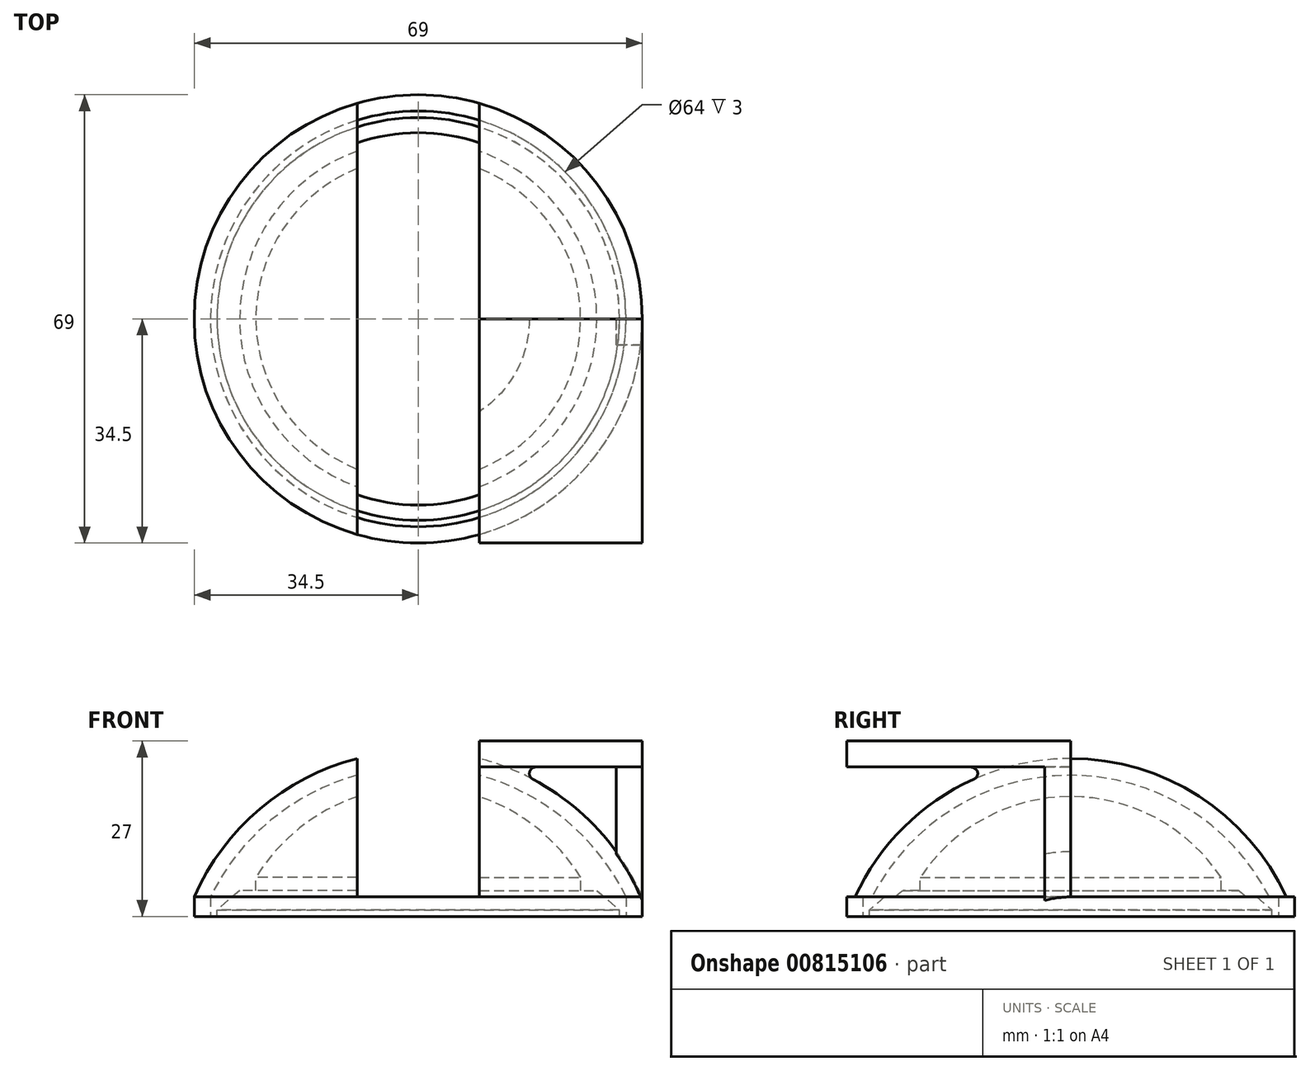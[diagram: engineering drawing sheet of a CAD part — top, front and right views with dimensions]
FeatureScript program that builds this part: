
annotation { "Feature Type Name" : "Feature", "Feature Type Description" : "" }
export const myFeature = defineFeature(function(context is Context, id is Id, definition is map)
    precondition{}
    {
        {
            var Q0;
            Q0=qCreatedBy(makeId("Front.planeOp"),FACE);
            var sketch = newSketch(context, id + "F0", { "sketchPlane" : qUnion([Q0])});
            skLineSegment(sketch, "E0", {"start": v(0, 0) * mm, "end": v(-31, 0) * mm});
            skLineSegment(sketch, "E1", {"start": v(-25, 4) * mm, "end": v(-27.5, 4) * mm});
            skLineSegment(sketch, "E2", {"start": v(-31, 0) * mm, "end": v(-31, 1) * mm});
            skLineSegment(sketch, "E3", {"start": v(-31, 1) * mm, "end": v(-27.5, 4) * mm});
            skLineSegment(sketch, "E4", {"start": v(-25, 4) * mm, "end": v(-25, 6) * mm});
            skArc(sketch, "E5.trimOffspring", {"start": v(0, 20) * mm, "mid": v(-14.33, 16.26) * mm, "end": v(-25, 6) * mm});
            skLineSegment(sketch, "E6", {"start": v(0, 20) * mm, "end": v(0, 0) * mm});
            skSolve(sketch);
        }
        {
            var Q0;
            Q0 = qSketchRegion(id + "F0", true);
            var Q1;
            Q1=sQuery(id+"F0.wireOp",EDGE,"E6");
            revolve(context, id + "F1", {"surfaceOperationType" : NewSurfaceOperationType.NEW, "entities" : qUnion([Q0]), "axis" : qUnion([Q1]), "revolveType" : RevolveType.FULL});
        }
        {
            var Q0;
            Q0=qCreatedBy(makeId("Top.planeOp"),FACE);
            var sketch = newSketch(context, id + "F2", { "sketchPlane" : qUnion([Q0])});
            skCircle(sketch, "E7", {"center": v(0, 0) * mm, "radius": 32 * mm});
            skCircle(sketch, "E8", {"center": v(0, 0) * mm, "radius": 34.5 * mm});
            skSolve(sketch);
        }
        {
            var Q0;
            Q0 = qSketchRegion(id + "F2", true);
            extrude(context, id + "F3", {"entities" : qUnion([Q0]), "depth" : 3 * mm, "offsetDistance" : 25 * mm});
        }
        {
            var Q0;
            Q0=qCreatedBy(makeId("Front.planeOp"),FACE);
            var sketch = newSketch(context, id + "F4", { "sketchPlane" : qUnion([Q0])});
            skLineSegment(sketch, "E9.0", {"start": v(-34.5, 3) * mm, "end": v(-32, 3) * mm});
            skArc(sketch, "E10", {"start": v(0, 23) * mm, "mid": v(-18.87, 17.59) * mm, "end": v(-32, 3) * mm});
            skLineSegment(sketch, "E11", {"start": v(0, 23) * mm, "end": v(0, 25.5) * mm});
            skArc(sketch, "E12", {"start": v(0, 25.5) * mm, "mid": v(-20.6, 19.38) * mm, "end": v(-34.5, 3) * mm});
            skPoint(sketch, "E13.0.end.orphan", {"position": v(32, 3) * mm});
            skPoint(sketch, "E14.trimOffspring.end.orphan", {"position": v(34.5, 3) * mm});
            skSolve(sketch);
        }
        {
            var Q0;
            Q0 = qSketchRegion(id + "F4", true);
            var Q1;
            Q1=sQuery(id+"F4.wireOp",EDGE,"E11");
            revolve(context, id + "F5", {"operationType" : NewBodyOperationType.ADD, "surfaceOperationType" : NewSurfaceOperationType.NEW, "entities" : qUnion([Q0]), "axis" : qUnion([Q1]), "revolveType" : RevolveType.FULL});
        }
        {
            var Q0;
            Q0=qCreatedBy(makeId("Top.planeOp"),FACE);
            cPlane(context, id + "F6", {"entities" : qUnion([Q0]), "cplaneType" : CPlaneType.OFFSET, "offset" : 27 * mm, "width" : 150 * mm, "height" : 150 * mm});
        }
        {
            var Q0;
            Q0=qCreatedBy(id+"F6.planeOp",FACE);
            var sketch = newSketch(context, id + "F7", { "sketchPlane" : qUnion([Q0])});
            skLineSegment(sketch, "E15", {"start": v(9.4, 0) * mm, "end": v(34.5, 0) * mm});
            skLineSegment(sketch, "E16", {"start": v(34.5, 0) * mm, "end": v(34.5, -34.5) * mm});
            skLineSegment(sketch, "E17", {"start": v(34.5, -34.5) * mm, "end": v(9.4, -34.5) * mm});
            skLineSegment(sketch, "E18", {"start": v(9.4, 0) * mm, "end": v(9.4, -34.5) * mm});
            skPoint(sketch, "E19.orphan", {"position": v(0, -34.5) * mm});
            skSolve(sketch);
        }
        {
            var Q0;
            Q0 = qSketchRegion(id + "F7", true);
            extrude(context, id + "F8", {"entities" : qUnion([Q0]), "operationType" : NewBodyOperationType.ADD, "oppositeDirection" : true, "depth" : 4 * mm, "offsetDistance" : 25 * mm});
        }
        {
            var Q0;
            Q0=makeQuery(id+"F8.opExtrude","CAP_FACE",FACE,{"disambiguationData":[OSD([sQuery(id+"F7.wireOp",EDGE,"E15"),sQuery(id+"F7.wireOp",EDGE,"E16"),sQuery(id+"F7.wireOp",EDGE,"E17"),sQuery(id+"F7.wireOp",EDGE,"E18")])],"isStart":false});
            var sketch = newSketch(context, id + "F9", { "sketchPlane" : qUnion([Q0])});
            skLineSegment(sketch, "E20.bottom", {"start": v(34.5, 0) * mm, "end": v(30.5, 0) * mm});
            skLineSegment(sketch, "E20.top", {"start": v(34.5, 4) * mm, "end": v(30.5, 4) * mm});
            skLineSegment(sketch, "E20.left", {"start": v(34.5, 0) * mm, "end": v(34.5, 4) * mm});
            skLineSegment(sketch, "E20.right", {"start": v(30.5, 0) * mm, "end": v(30.5, 4) * mm});
            skSolve(sketch);
        }
        {
            var Q0;
            Q0 = qSketchRegion(id + "F9", true);
            var Q1;
            Q1=makeQuery(id+"F5.opRevolve","SWEPT_FACE",FACE,{"disambiguationData":[OSD([sQuery(id+"F4.wireOp",EDGE,"E12")])]});
            extrude(context, id + "F10", {"entities" : qUnion([Q0]), "operationType" : NewBodyOperationType.ADD, "endBound" : BoundingType.UP_TO_SURFACE, "depth" : 25 * mm, "endBoundEntityFace" : qUnion([Q1]), "offsetDistance" : 25 * mm});
        }
        {
            var Q0;
            Q0=qCreatedBy(id+"F6.planeOp",FACE);
            var sketch = newSketch(context, id + "F11", { "sketchPlane" : qUnion([Q0])});
            skPoint(sketch, "E21.0", {"position": v(9.4, 0) * mm});
            skLineSegment(sketch, "E22.bottom", {"start": v(9.4, 40.92) * mm, "end": v(-9.4, 40.92) * mm});
            skLineSegment(sketch, "E22.top", {"start": v(9.4, -40.92) * mm, "end": v(-9.4, -40.92) * mm});
            skLineSegment(sketch, "E22.left", {"start": v(9.4, 40.92) * mm, "end": v(9.4, -40.92) * mm});
            skLineSegment(sketch, "E22.right", {"start": v(-9.4, 40.92) * mm, "end": v(-9.4, -40.92) * mm});
            skPoint(sketch, "E22.middle", {"position": v(0, 0) * mm});
            skSolve(sketch);
        }
        {
            var Q0;
            Q0 = qSketchRegion(id + "F11", true);
            var Q1;
            Q1=makeQuery(id+"F10.opExtrude","CAP_VERTEX",VERTEX,{"disambiguationData":[OSD([sQuery(id+"F4.wireOp",EDGE,"E12"),sQuery(id+"F9.wireOp",EDGE,"E20.bottom"),sQuery(id+"F9.wireOp",EDGE,"E20.left")])],"isStart":false});
            extrude(context, id + "F12", {"entities" : qUnion([Q0]), "operationType" : NewBodyOperationType.REMOVE, "endBound" : BoundingType.UP_TO_VERTEX, "oppositeDirection" : true, "depth" : 25 * mm, "endBoundEntityVertex" : qUnion([Q1]), "offsetDistance" : 25 * mm});
        }
        {
            var Q0;
            Q0=makeQuery(id+"F8.boolean.opBoolean","INTERSECT",EDGE,{"derivedFrom":[makeQuery(id+"F5.opRevolve","SWEPT_FACE",FACE,{"disambiguationData":[OSD([sQuery(id+"F4.wireOp",EDGE,"E12")])]}),makeQuery(id+"F8.opExtrude","CAP_FACE",FACE,{"disambiguationData":[OSD([sQuery(id+"F7.wireOp",EDGE,"E15"),sQuery(id+"F7.wireOp",EDGE,"E16"),sQuery(id+"F7.wireOp",EDGE,"E17"),sQuery(id+"F7.wireOp",EDGE,"E18")])],"isStart":false})]});
            fillet(context, id + "F13", {"entities" : qUnion([Q0]), "radius" : 1 * mm, "tangentPropagation" : true, "allowEdgeOverflow" : false});
        }
    });
